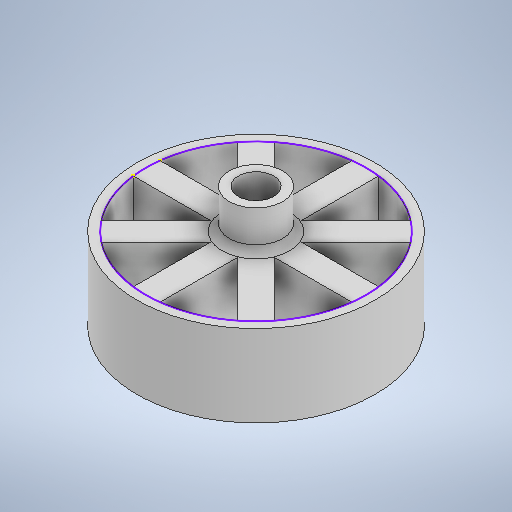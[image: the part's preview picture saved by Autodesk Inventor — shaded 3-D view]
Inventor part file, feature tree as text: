
AUTODESK INVENTOR PART (.ipt)
format: ipt  version: 2025.2 (Build 292293000, 293)  size: 355,328 bytes
history: native  units: mm
features: sketch x9, extrude x5, hole x2, fillet x1
ambient origin geometry x8: Origin, YZ Plane, XZ Plane, XY Plane, X Axis, Y Axis, Z Axis, Center Point
bodies: Solid1 (feature_tree)
feature tree (17):
  extrude  "Extrusion1"  Depth=67.0mm
  hole  "Hole1"  [1 undecoded]
  hole  "Hole2"  [1 undecoded]
  extrude  "Extrusion3"  Depth=10.0mm
  extrude  "Extrusion4"  Depth=11.0mm TaperAngle=360.0deg
  extrude  "Extrusion5"  Depth=2.0mm
  extrude  "Extrusion6"  Depth=5.0mm
  sketch  "Sketch9"  dims[d62=0.872665mm d63=5.0mm d64=0.872665mm]
  fillet  "Fillet2"  Radius=0.872665mm
  sketch  "Sketch1"  dims[d0=62.0mm d1=67.0mm]
  sketch  "Sketch3"  dims[d29=62.0mm d30=7.5mm d31=3.75mm d32=2.5mm d33=90.0deg d34=10.0mm d35=20.594885mm]
  sketch  "Sketch4"  dims[d39=62.0mm d40=7.5mm d41=3.75mm d42=2.5mm d43=90.0deg d44=10.0mm d45=20.594885mm d46=10.0mm]
  sketch  "Sketch5"  dims[d47=23.0mm d48=0.0mm d49=15.0mm]
  sketch  "Sketch6"  dims[d50=23.0mm d51=0.0mm d52=10.0mm]
  sketch  "Sketch7"  dims[d53=11.0mm d54=0.0mm d55=80.0mm d57=360.0deg]
  sketch  "Sketch8"  dims[d59=23.0mm d60=0.0mm d61=2.0mm]
  sketch  "Sketch Circular Pattern1"  dims[d2=23.0mm d3=0.0mm]
note: 2 required parameter values undecoded (feature->parameter linkage not recoverable at this tier; creation-order binding heuristic only, values carry confidence <= 0.55)
